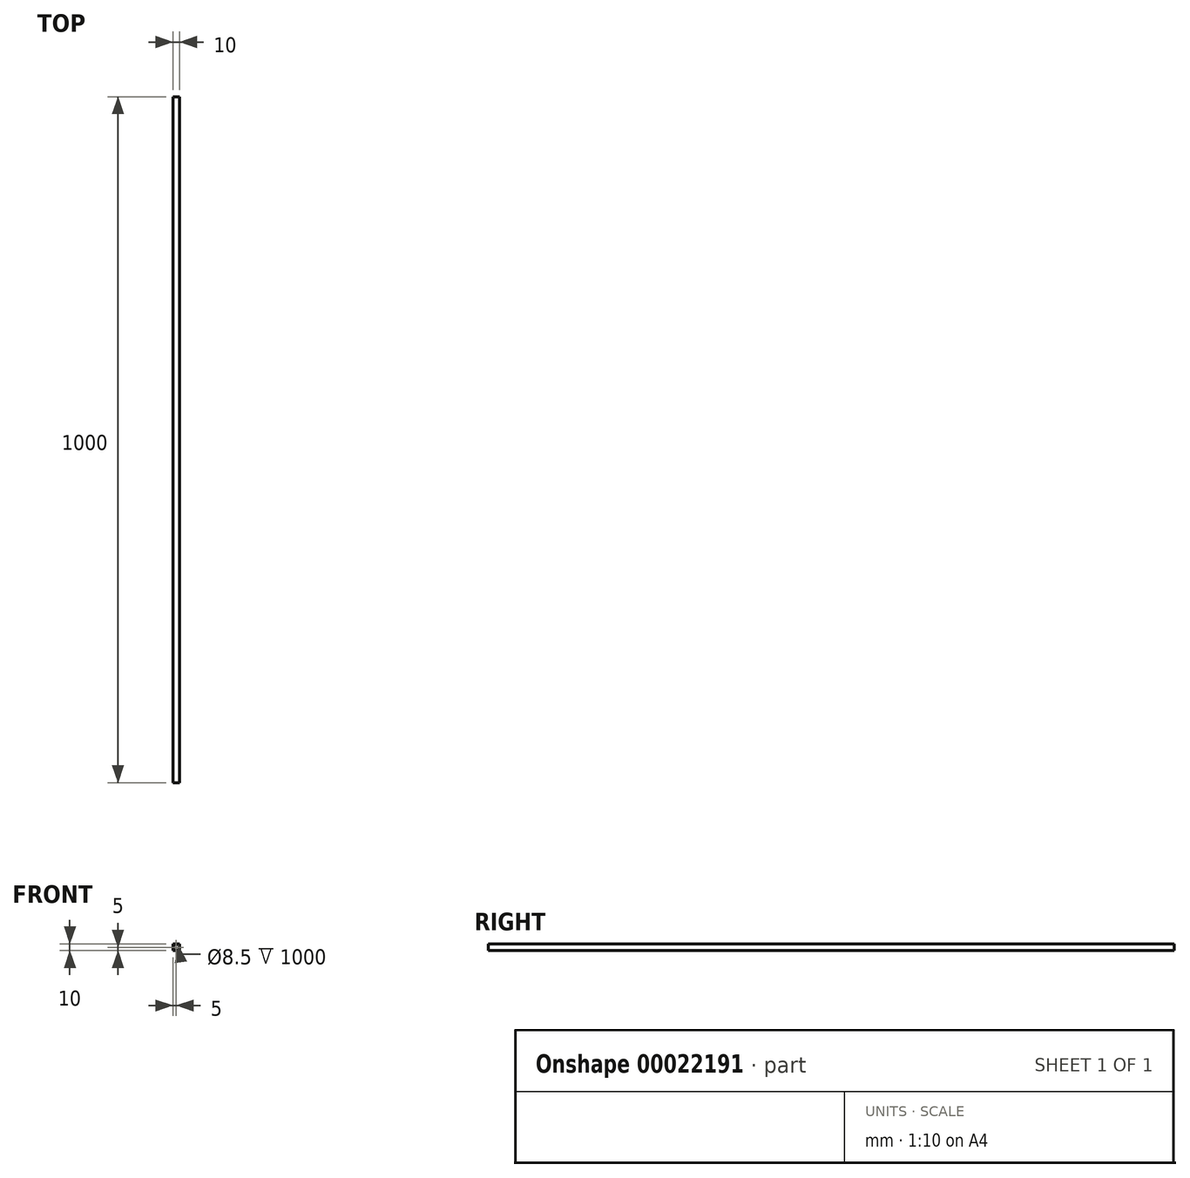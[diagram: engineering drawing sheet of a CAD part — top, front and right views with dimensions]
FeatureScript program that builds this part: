
annotation { "Feature Type Name" : "Feature", "Feature Type Description" : "" }
export const myFeature = defineFeature(function(context is Context, id is Id, definition is map)
    precondition{}
    {
        {
            var Q0;
            Q0=qCreatedBy(makeId("Front.planeOp"),FACE);
            var sketch = newSketch(context, id + "F0", { "sketchPlane" : qUnion([Q0])});
            skLineSegment(sketch, "E0.rect.bottom", {"start": v(5, -5) * mm, "end": v(-5, -5) * mm});
            skLineSegment(sketch, "E0.rect.top", {"start": v(5, 5) * mm, "end": v(-5, 5) * mm});
            skLineSegment(sketch, "E0.rect.left", {"start": v(5, -5) * mm, "end": v(5, 5) * mm});
            skLineSegment(sketch, "E0.rect.right", {"start": v(-5, -5) * mm, "end": v(-5, 5) * mm});
            skPoint(sketch, "E0.rect.middle", {"position": v(0, 0) * mm});
            skCircle(sketch, "E1", {"center": v(0, 0) * mm, "radius": 4.25 * mm});
            skSolve(sketch);
        }
        {
            var Q0;
            Q0 = qSketchRegion(id + "F0", true);
            extrude(context, id + "F1", {"entities" : qUnion([Q0]), "depth" : 1000 * mm});
        }
    });
